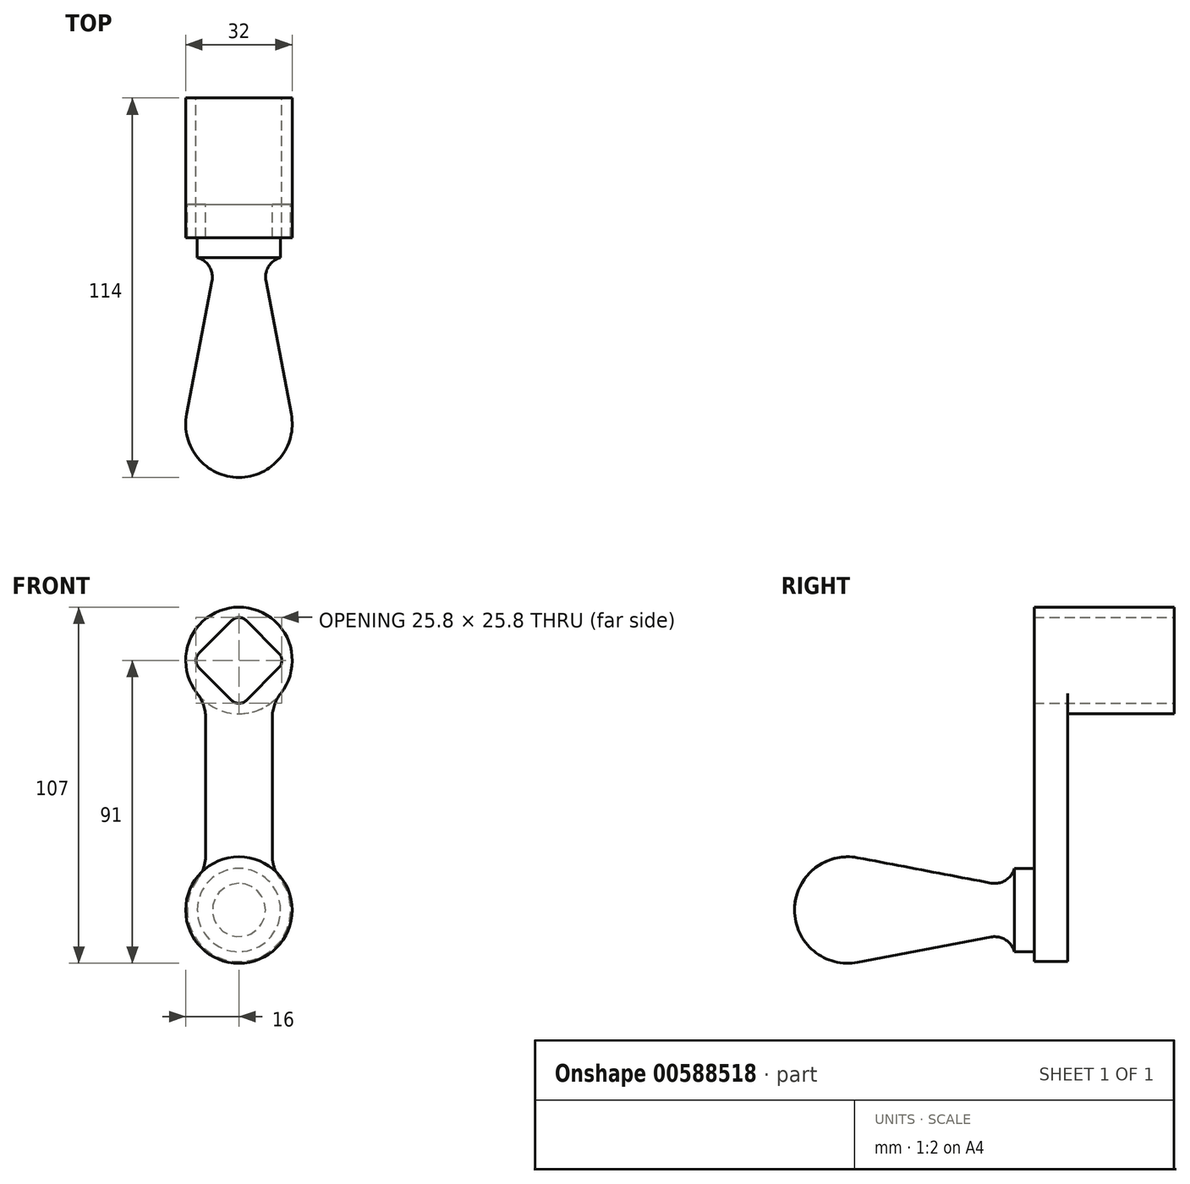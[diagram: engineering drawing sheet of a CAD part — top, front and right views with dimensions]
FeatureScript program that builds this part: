
annotation { "Feature Type Name" : "Feature", "Feature Type Description" : "" }
export const myFeature = defineFeature(function(context is Context, id is Id, definition is map)
    precondition{}
    {
        {
            var Q0;
            Q0=qCreatedBy(makeId("Front.planeOp"),FACE);
            var sketch = newSketch(context, id + "F0", { "sketchPlane" : qUnion([Q0])});
            skArc(sketch, "E0", {"start": v(-12.4, 9.3) * mm, "mid": v(0, -15.5) * mm, "end": v(12.4, 9.3) * mm});
            skLineSegment(sketch, "E1", {"start": v(-10, 16.5) * mm, "end": v(-10, 57.68) * mm});
            skArc(sketch, "E2", {"start": v(12.57, 65.1) * mm, "mid": v(0, 91) * mm, "end": v(-12.57, 65.1) * mm});
            skLineSegment(sketch, "E3", {"start": v(10, 57.68) * mm, "end": v(10, 16.5) * mm});
            skPoint(sketch, "E4.visualSharp", {"position": v(10, 62.51) * mm});
            skArc(sketch, "E4.filletArc", {"start": v(12.57, 65.1) * mm, "mid": v(10.66, 61.6) * mm, "end": v(10, 57.68) * mm});
            skPoint(sketch, "E5.visualSharp", {"position": v(-10, 62.51) * mm});
            skArc(sketch, "E5.filletArc", {"start": v(-10, 57.68) * mm, "mid": v(-10.66, 61.6) * mm, "end": v(-12.57, 65.1) * mm});
            skPoint(sketch, "E6.visualSharp", {"position": v(-10, 11.84) * mm});
            skArc(sketch, "E6.filletArc", {"start": v(-12.4, 9.3) * mm, "mid": v(-10.62, 12.7) * mm, "end": v(-10, 16.5) * mm});
            skPoint(sketch, "E7.visualSharp", {"position": v(10, 11.84) * mm});
            skArc(sketch, "E7.filletArc", {"start": v(10, 16.5) * mm, "mid": v(10.62, 12.7) * mm, "end": v(12.4, 9.3) * mm});
            skLineSegment(sketch, "E8", {"start": v(12.02, 77.12) * mm, "end": v(2.12, 87.02) * mm});
            skLineSegment(sketch, "E9", {"start": v(-12.02, 77.12) * mm, "end": v(-2.12, 87.02) * mm});
            skLineSegment(sketch, "E10", {"start": v(-12.02, 72.88) * mm, "end": v(-2.12, 62.98) * mm});
            skLineSegment(sketch, "E11", {"start": v(12.02, 72.88) * mm, "end": v(2.12, 62.98) * mm});
            skPoint(sketch, "E12.visualSharp", {"position": v(0, 89.14) * mm});
            skArc(sketch, "E12.filletArc", {"start": v(2.12, 87.02) * mm, "mid": v(0, 87.9) * mm, "end": v(-2.12, 87.02) * mm});
            skPoint(sketch, "E13.visualSharp", {"position": v(14.14, 75) * mm});
            skArc(sketch, "E13.filletArc", {"start": v(12.02, 72.88) * mm, "mid": v(12.9, 75) * mm, "end": v(12.02, 77.12) * mm});
            skPoint(sketch, "E14.visualSharp", {"position": v(0, 60.86) * mm});
            skArc(sketch, "E14.filletArc", {"start": v(-2.12, 62.98) * mm, "mid": v(0, 62.1) * mm, "end": v(2.12, 62.98) * mm});
            skPoint(sketch, "E15.visualSharp", {"position": v(-14.14, 75) * mm});
            skArc(sketch, "E15.filletArc", {"start": v(-12.02, 77.12) * mm, "mid": v(-12.9, 75) * mm, "end": v(-12.02, 72.88) * mm});
            skCircle(sketch, "E16", {"center": v(0, 75) * mm, "radius": 16 * mm});
            skSolve(sketch);
        }
        {
            var Q0;
            Q0=makeQuery(id+"F0.imprint","IMPRINT",FACE,{"disambiguationData":[TD([[makeQuery(id+"F0.imprint","IMPRINT",EDGE,{"derivedFrom":sQuery(id+"F0.wireOp",EDGE,"E8")}),-1.0]])]});
            var Q1;
            Q1=makeQuery(id+"F0.imprint","IMPRINT",FACE,{"disambiguationData":[TD([[makeQuery(id+"F0.imprint","IMPRINT",EDGE,{"derivedFrom":sQuery(id+"F0.wireOp",EDGE,"E0")}),1.0]])]});
            extrude(context, id + "F1", {"entities" : qUnion([Q0, Q1]), "depth" : 10 * mm, "offsetDistance" : 25 * mm});
        }
        {
            var Q0;
            Q0=makeQuery(id+"F0.imprint","IMPRINT",FACE,{"disambiguationData":[TD([[makeQuery(id+"F0.imprint","IMPRINT",EDGE,{"derivedFrom":sQuery(id+"F0.wireOp",EDGE,"E8")}),-1.0]])]});
            extrude(context, id + "F2", {"entities" : qUnion([Q0]), "operationType" : NewBodyOperationType.ADD, "oppositeDirection" : true, "depth" : 32 * mm, "offsetDistance" : 25 * mm});
        }
        {
            var Q0;
            Q0=qCreatedBy(makeId("Right.planeOp"),FACE);
            var sketch = newSketch(context, id + "F3", { "sketchPlane" : qUnion([Q0])});
            skLineSegment(sketch, "E17", {"start": v(0, 0) * mm, "end": v(-66, 0) * mm});
            skArc(sketch, "E18", {"start": v(-63.01, 15.72) * mm, "mid": v(-76.2, 12.32) * mm, "end": v(-82, 0) * mm});
            skLineSegment(sketch, "E19", {"start": v(-10, 0) * mm, "end": v(-10, 12.5) * mm});
            skLineSegment(sketch, "E20", {"start": v(-10, 12.5) * mm, "end": v(-16, 12.5) * mm});
            skArc(sketch, "E21", {"start": v(-22.93, 8.1) * mm, "mid": v(-18.6, 8.93) * mm, "end": v(-16, 12.5) * mm});
            skLineSegment(sketch, "E22", {"start": v(-22.93, 8.1) * mm, "end": v(-63.01, 15.72) * mm});
            skLineSegment(sketch, "E23", {"start": v(-66, 0) * mm, "end": v(-82, 0) * mm});
            skSolve(sketch);
        }
        {
            var Q0;
            Q0=makeQuery(id+"F3.imprint","IMPRINT",FACE,{"disambiguationData":[TD([[makeQuery(id+"F3.imprint","IMPRINT",EDGE,{"derivedFrom":sQuery(id+"F3.wireOp",EDGE,"E18")}),1.0]])]});
            var Q1;
            Q1=sQuery(id+"F3.wireOp",EDGE,"E17");
            revolve(context, id + "F4", {"operationType" : NewBodyOperationType.ADD, "entities" : qUnion([Q0]), "axis" : qUnion([Q1]), "revolveType" : RevolveType.FULL});
        }
    });
